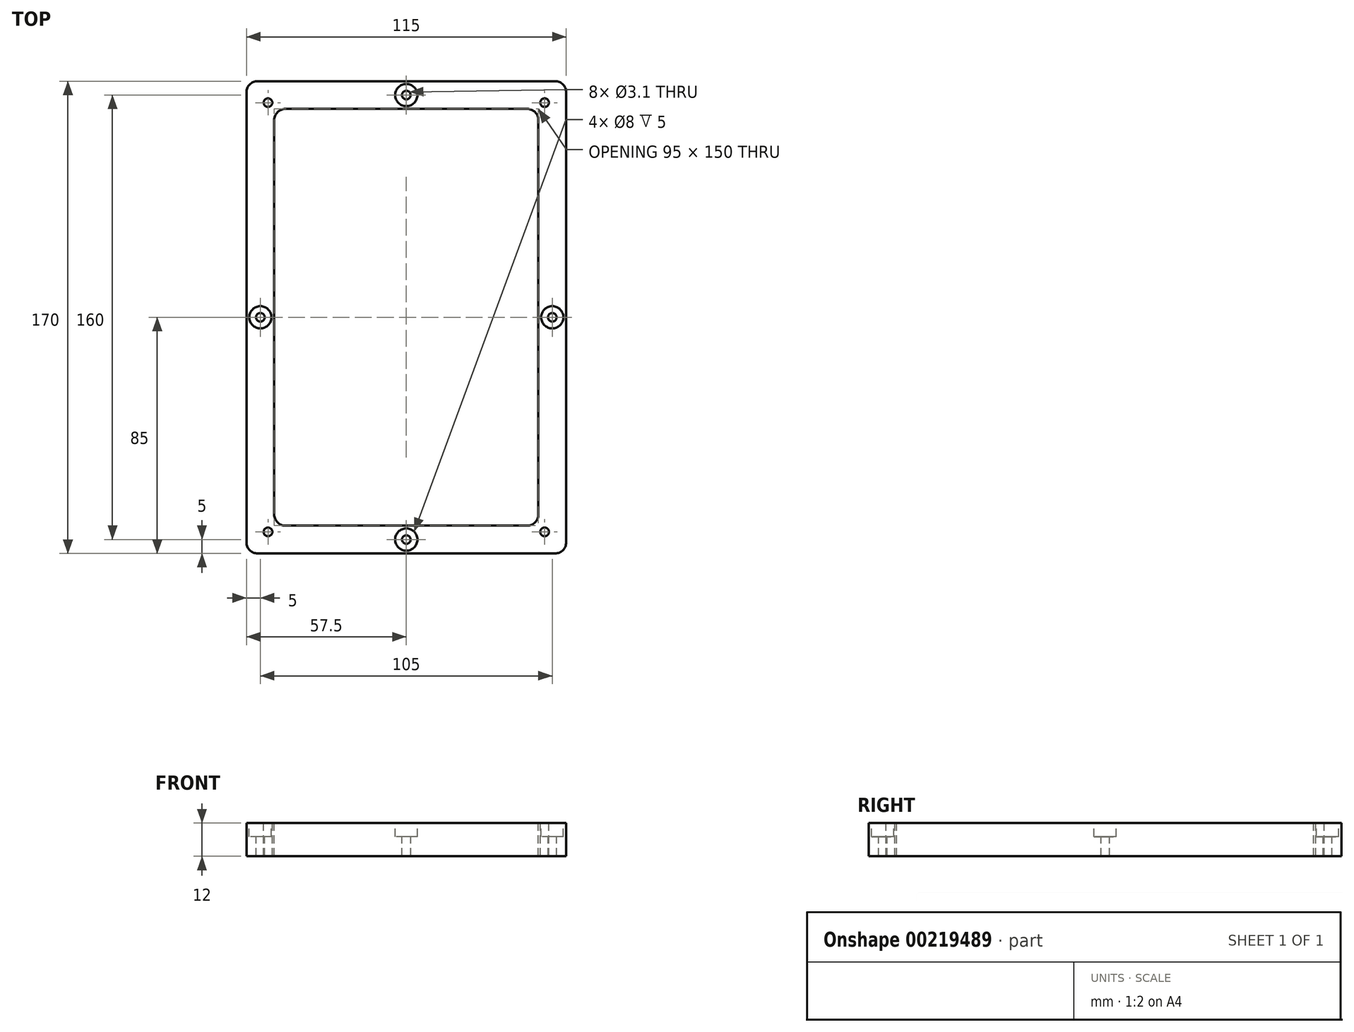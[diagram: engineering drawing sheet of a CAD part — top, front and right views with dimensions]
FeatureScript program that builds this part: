
annotation { "Feature Type Name" : "Feature", "Feature Type Description" : "" }
export const myFeature = defineFeature(function(context is Context, id is Id, definition is map)
    precondition{}
    {
        {
            var Q0;
            Q0=qCreatedBy(makeId("Top.planeOp"),FACE);
            var sketch = newSketch(context, id + "F0", { "sketchPlane" : qUnion([Q0])});
            skLineSegment(sketch, "E0.bottom", {"start": v(-57.5, 85) * mm, "end": v(57.5, 85) * mm});
            skLineSegment(sketch, "E0.top", {"start": v(-57.5, -85) * mm, "end": v(57.5, -85) * mm});
            skLineSegment(sketch, "E0.left", {"start": v(-57.5, 85) * mm, "end": v(-57.5, -85) * mm});
            skLineSegment(sketch, "E0.right", {"start": v(57.5, 85) * mm, "end": v(57.5, -85) * mm});
            skSolve(sketch);
        }
        {
            var Q0;
            Q0=qSketchRegion(id+"F0",true);
            extrude(context, id + "F1", {"entities" : qUnion([Q0]), "depth" : 12 * mm});
        }
        {
            var Q0;
            Q0=makeQuery(id+"F1.opExtrude","CAP_FACE",FACE,{"disambiguationData":[OSD([sQuery(id+"F0.wireOp",EDGE,"E0.bottom"),sQuery(id+"F0.wireOp",EDGE,"E0.top"),sQuery(id+"F0.wireOp",EDGE,"E0.left"),sQuery(id+"F0.wireOp",EDGE,"E0.right")])],"isStart":false});
            var sketch = newSketch(context, id + "F2", { "sketchPlane" : qUnion([Q0])});
            skLineSegment(sketch, "E1.bottom", {"start": v(-47.5, 75) * mm, "end": v(47.5, 75) * mm});
            skLineSegment(sketch, "E1.top", {"start": v(-47.5, -75) * mm, "end": v(47.5, -75) * mm});
            skLineSegment(sketch, "E1.left", {"start": v(-47.5, 75) * mm, "end": v(-47.5, -75) * mm});
            skLineSegment(sketch, "E1.right", {"start": v(47.5, 75) * mm, "end": v(47.5, -75) * mm});
            skSolve(sketch);
        }
        {
            var Q0;
            Q0=qSketchRegion(id+"F2",true);
            extrude(context, id + "F3", {"entities" : qUnion([Q0]), "operationType" : NewBodyOperationType.REMOVE, "endBound" : BoundingType.THROUGH_ALL, "oppositeDirection" : true, "depth" : 25 * mm});
        }
        {
            var Q0;
            Q0=makeQuery(id+"F1.opExtrude","CAP_FACE",FACE,{"disambiguationData":[OSD([sQuery(id+"F0.wireOp",EDGE,"E0.bottom"),sQuery(id+"F0.wireOp",EDGE,"E0.top"),sQuery(id+"F0.wireOp",EDGE,"E0.left"),sQuery(id+"F0.wireOp",EDGE,"E0.right")])],"isStart":false});
            var sketch = newSketch(context, id + "F4", { "sketchPlane" : qUnion([Q0])});
            skCircle(sketch, "E2", {"center": v(0, 80) * mm, "radius": 1.55 * mm});
            skPoint(sketch, "E2.centerSnap0", {"position": v(0, 75) * mm});
            skCircle(sketch, "E3", {"center": v(0, -80) * mm, "radius": 1.55 * mm});
            skPoint(sketch, "E3.centerSnap0", {"position": v(0, -85) * mm});
            skCircle(sketch, "E4", {"center": v(52.5, 0) * mm, "radius": 1.55 * mm});
            skPoint(sketch, "E4.centerSnap0", {"position": v(47.5, 0) * mm});
            skCircle(sketch, "E5", {"center": v(-52.5, 0) * mm, "radius": 1.55 * mm});
            skPoint(sketch, "E5.centerSnap0", {"position": v(-47.5, 0) * mm});
            skLineSegment(sketch, "E6", {"start": v(-47.5, 0) * mm, "end": v(-57.5, 0) * mm, "construction": true});
            skLineSegment(sketch, "E7", {"start": v(47.5, 0) * mm, "end": v(57.5, 0) * mm, "construction": true});
            skLineSegment(sketch, "E8", {"start": v(0, 75) * mm, "end": v(0, 85) * mm, "construction": true});
            skLineSegment(sketch, "E9", {"start": v(0, -75) * mm, "end": v(0, -85) * mm, "construction": true});
            skSolve(sketch);
        }
        {
            var Q0;
            Q0=qSketchRegion(id+"F4",true);
            extrude(context, id + "F5", {"entities" : qUnion([Q0]), "operationType" : NewBodyOperationType.REMOVE, "endBound" : BoundingType.THROUGH_ALL, "oppositeDirection" : true, "depth" : 25 * mm});
        }
        {
            var Q0;
            Q0=makeQuery(id+"F3.boolean.opBoolean","COPY",EDGE,{"derivedFrom":makeQuery(id+"F3.opExtrude","SWEPT_EDGE",EDGE,{"disambiguationData":[OSD([sQuery(id+"F2.wireOp",EDGE,"E1.bottom"),sQuery(id+"F2.wireOp",EDGE,"E1.right")])]})});
            var Q1;
            Q1=makeQuery(id+"F3.boolean.opBoolean","COPY",EDGE,{"derivedFrom":makeQuery(id+"F3.opExtrude","SWEPT_EDGE",EDGE,{"disambiguationData":[OSD([sQuery(id+"F2.wireOp",EDGE,"E1.bottom"),sQuery(id+"F2.wireOp",EDGE,"E1.left")])]})});
            var Q2;
            Q2=makeQuery(id+"F1.opExtrude","SWEPT_EDGE",EDGE,{"disambiguationData":[OSD([sQuery(id+"F0.wireOp",EDGE,"E0.bottom"),sQuery(id+"F0.wireOp",EDGE,"E0.right")])]});
            var Q3;
            Q3=makeQuery(id+"F1.opExtrude","SWEPT_EDGE",EDGE,{"disambiguationData":[OSD([sQuery(id+"F0.wireOp",EDGE,"E0.top"),sQuery(id+"F0.wireOp",EDGE,"E0.right")])]});
            var Q4;
            Q4=makeQuery(id+"F1.opExtrude","SWEPT_EDGE",EDGE,{"disambiguationData":[OSD([sQuery(id+"F0.wireOp",EDGE,"E0.top"),sQuery(id+"F0.wireOp",EDGE,"E0.left")])]});
            var Q5;
            Q5=makeQuery(id+"F1.opExtrude","SWEPT_EDGE",EDGE,{"disambiguationData":[OSD([sQuery(id+"F0.wireOp",EDGE,"E0.bottom"),sQuery(id+"F0.wireOp",EDGE,"E0.left")])]});
            var Q6;
            Q6=makeQuery(id+"F3.boolean.opBoolean","COPY",EDGE,{"derivedFrom":makeQuery(id+"F3.opExtrude","SWEPT_EDGE",EDGE,{"disambiguationData":[OSD([sQuery(id+"F2.wireOp",EDGE,"E1.top"),sQuery(id+"F2.wireOp",EDGE,"E1.right")])]})});
            var Q7;
            Q7=makeQuery(id+"F3.boolean.opBoolean","COPY",EDGE,{"derivedFrom":makeQuery(id+"F3.opExtrude","SWEPT_EDGE",EDGE,{"disambiguationData":[OSD([sQuery(id+"F2.wireOp",EDGE,"E1.top"),sQuery(id+"F2.wireOp",EDGE,"E1.left")])]})});
            fillet(context, id + "F6", {"entities" : qUnion([Q0, Q1, Q2, Q3, Q4, Q5, Q6, Q7]), "radius" : 4 * mm, "tangentPropagation" : true, "allowEdgeOverflow" : false});
        }
        {
            var Q0;
            Q0=makeQuery(id+"F1.opExtrude","CAP_FACE",FACE,{"disambiguationData":[OSD([sQuery(id+"F0.wireOp",EDGE,"E0.bottom"),sQuery(id+"F0.wireOp",EDGE,"E0.top"),sQuery(id+"F0.wireOp",EDGE,"E0.left"),sQuery(id+"F0.wireOp",EDGE,"E0.right")])],"isStart":false});
            var sketch = newSketch(context, id + "F7", { "sketchPlane" : qUnion([Q0])});
            skCircle(sketch, "E10", {"center": v(-49.75, 77.25) * mm, "radius": 1.55 * mm});
            skCircle(sketch, "E11", {"center": v(49.75, 77.25) * mm, "radius": 1.55 * mm});
            skCircle(sketch, "E12", {"center": v(49.75, -77.25) * mm, "radius": 1.55 * mm});
            skCircle(sketch, "E13", {"center": v(-49.75, -77.25) * mm, "radius": 1.55 * mm});
            skSolve(sketch);
        }
        {
            var Q0;
            Q0=qSketchRegion(id+"F7",true);
            extrude(context, id + "F8", {"entities" : qUnion([Q0]), "operationType" : NewBodyOperationType.REMOVE, "endBound" : BoundingType.THROUGH_ALL, "oppositeDirection" : true, "depth" : 25 * mm});
        }
        {
            var Q0;
            Q0=makeQuery(id+"F1.opExtrude","CAP_FACE",FACE,{"disambiguationData":[OSD([sQuery(id+"F0.wireOp",EDGE,"E0.bottom"),sQuery(id+"F0.wireOp",EDGE,"E0.top"),sQuery(id+"F0.wireOp",EDGE,"E0.left"),sQuery(id+"F0.wireOp",EDGE,"E0.right")])],"isStart":false});
            var sketch = newSketch(context, id + "F9", { "sketchPlane" : qUnion([Q0])});
            skCircle(sketch, "E14", {"center": v(0, 80) * mm, "radius": 4 * mm});
            skPoint(sketch, "E15.startSnap0", {"position": v(0, 85) * mm});
            skCircle(sketch, "E16", {"center": v(-52.5, 0) * mm, "radius": 4 * mm});
            skCircle(sketch, "E17", {"center": v(0, -80) * mm, "radius": 4 * mm});
            skCircle(sketch, "E18", {"center": v(52.5, 0) * mm, "radius": 4 * mm});
            skSolve(sketch);
        }
        {
            var Q0;
            Q0 = qSketchRegion(id + "F9", true);
            extrude(context, id + "F10", {"entities" : qUnion([Q0]), "operationType" : NewBodyOperationType.REMOVE, "oppositeDirection" : true, "depth" : 5 * mm});
        }
    });
